# Revit family: WSL_A3-Skylight-Peaked-SMARTBIM
name_source: partatom
category: Windows
revit_build: Autodesk Revit 2016 (Build: 20150220_1215(x64)
units: mm (PartAtom-declared; Revit-internal decimal feet)

## family parameters
Always vertical = No
Cut with Voids When Loaded = No
Host = Roof
Room Calculation Point = No
Shared = No

## types (1)
- Parametric
    # of Mullions = 6
    04 CSI = 08 60 00
    95 CSI = 08600
    Assembly Code = B3020110
    Curb Depth = 0' - 3 1/2"
    Curb Height = 0' - 5"
    Frame = Metal Aluminium
    Frame Height = 0' - 3 1/2"
    Glass = Glass
    Height = 0' - 6"
    Length = 3' - 0"
    Manufacturer = SMARTBIM
    Mullion = Mullion Material
    Mullion Side Length = 0' - 1"
    Mullion Side Length Note = Only 1 inch
    Mullion Spacing = 0' - 6"
    Mullion Width = 3' - 1"
    Peak Height = 2' - 0"
    SmartBIM Object Version = 3
    Subcategory = Skylight
    Total Frame Height = 0' - 8 1/2"
    Width = 3' - 0"

## geometry (parser evidence)
native form markers: Extrusion x1, Sweep x7
no freeform markers — native parametric forms only
